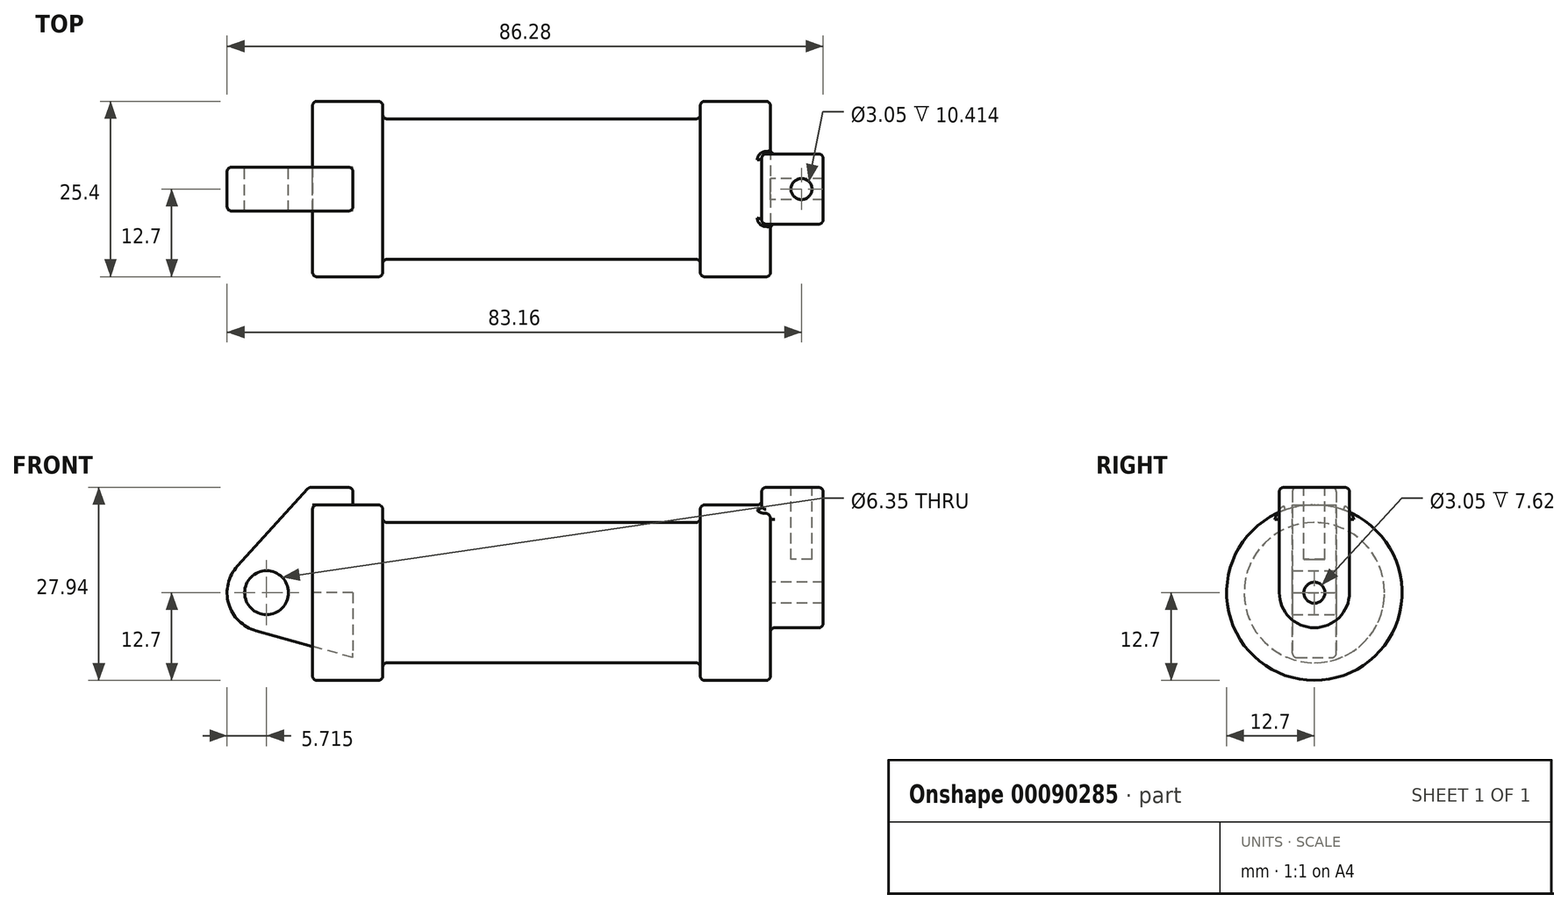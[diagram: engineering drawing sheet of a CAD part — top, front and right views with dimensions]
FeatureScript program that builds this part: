
annotation { "Feature Type Name" : "Feature", "Feature Type Description" : "" }
export const myFeature = defineFeature(function(context is Context, id is Id, definition is map)
    precondition{}
    {
        {
            var Q0;
            Q0=qCreatedBy(makeId("Front.planeOp"),FACE);
            var sketch = newSketch(context, id + "F0", { "sketchPlane" : qUnion([Q0])});
            skLineSegment(sketch, "E0", {"start": v(0, 0) * mm, "end": v(0, 12.7) * mm});
            skLineSegment(sketch, "E1", {"start": v(0, 12.7) * mm, "end": v(10.16, 12.7) * mm});
            skLineSegment(sketch, "E2", {"start": v(10.16, 12.7) * mm, "end": v(10.16, 10.16) * mm});
            skLineSegment(sketch, "E3", {"start": v(10.16, 10.16) * mm, "end": v(56.13, 10.16) * mm});
            skLineSegment(sketch, "E4", {"start": v(56.13, 10.16) * mm, "end": v(56.13, 12.7) * mm});
            skLineSegment(sketch, "E5", {"start": v(56.13, 12.7) * mm, "end": v(66.3, 12.7) * mm});
            skLineSegment(sketch, "E6", {"start": v(66.3, 12.7) * mm, "end": v(66.3, 0) * mm});
            skLineSegment(sketch, "E7", {"start": v(66.3, 0) * mm, "end": v(0, 0) * mm});
            skLineSegment(sketch, "E8", {"start": v(5.84, 15.24) * mm, "end": v(-0.5, 15.24) * mm});
            skLineSegment(sketch, "E9", {"start": v(-0.5, 15.24) * mm, "end": v(-10.88, 3.85) * mm});
            skLineSegment(sketch, "E10", {"start": v(0, 0) * mm, "end": v(-6.65, 0) * mm});
            skCircle(sketch, "E11", {"center": v(-6.65, 0) * mm, "radius": 5.72 * mm});
            skCircle(sketch, "E12", {"center": v(-6.65, 0) * mm, "radius": 3.18 * mm});
            skLineSegment(sketch, "E13", {"start": v(5.84, 15.24) * mm, "end": v(5.84, -9.4) * mm});
            skLineSegment(sketch, "E14", {"start": v(5.84, -9.4) * mm, "end": v(-8.18, -5.5) * mm});
            skSolve(sketch);
        }
        {
            var Q0;
            {var subQ0=sQuery(id+"F0.wireOp",EDGE,"E0");Q0=makeQuery(id+"F0.imprint","IMPRINT",FACE,{"disambiguationData":[TD([[makeQuery(id+"F0.imprint","IMPRINT",EDGE,{"derivedFrom":subQ0}),-1.0]])]});}
            var Q1;
            {var subQ0=sQuery(id+"F0.wireOp",EDGE,"E2");Q1=makeQuery(id+"F0.imprint","IMPRINT",FACE,{"disambiguationData":[TD([[makeQuery(id+"F0.imprint","IMPRINT",EDGE,{"derivedFrom":subQ0}),-1.0]])]});}
            var Q2;
            Q2=sQuery(id+"F0.wireOp",EDGE,"E7");
            revolve(context, id + "F1", {"entities" : qUnion([Q0, Q1]), "axis" : qUnion([Q2]), "revolveType" : RevolveType.FULL});
        }
        {
            var Q0;
            Q0=makeQuery(id+"F1.opRevolve","SWEPT_FACE",FACE,{"disambiguationData":[OSD([sQuery(id+"F0.wireOp",EDGE,"E6")])]});
            var sketch = newSketch(context, id + "F2", { "sketchPlane" : qUnion([Q0])});
            skCircle(sketch, "E15", {"center": v(0, 0) * mm, "radius": 1.52 * mm});
            skCircle(sketch, "E16", {"center": v(0, 0) * mm, "radius": 5.08 * mm});
            skLineSegment(sketch, "E17", {"start": v(-5.08, 0) * mm, "end": v(-5.08, 15.24) * mm});
            skLineSegment(sketch, "E18", {"start": v(5.08, 0) * mm, "end": v(5.08, 15.24) * mm});
            skLineSegment(sketch, "E19", {"start": v(-5.08, 15.24) * mm, "end": v(5.08, 15.24) * mm});
            skSolve(sketch);
        }
        {
            var Q0;
            Q0 = qSketchRegion(id + "F2", true);
            extrude(context, id + "F3", {"entities" : qUnion([Q0]), "operationType" : NewBodyOperationType.ADD, "depth" : 7.62 * mm});
        }
        {
            var Q0;
            Q0=makeQuery(id+"F3.opExtrude","CAP_FACE",FACE,{"disambiguationData":[OSD([sQuery(id+"F2.wireOp",EDGE,"E15"),sQuery(id+"F2.wireOp",EDGE,"E16"),sQuery(id+"F2.wireOp",EDGE,"E17"),sQuery(id+"F2.wireOp",EDGE,"E18"),sQuery(id+"F2.wireOp",EDGE,"E19")])],"isStart":true});
            extrude(context, id + "F4", {"entities" : qUnion([Q0]), "operationType" : NewBodyOperationType.ADD, "depth" : 1.27 * mm});
        }
        {
            var Q0;
            {var subQ0=sQuery(id+"F2.wireOp",EDGE,"E19");Q0=makeQuery(id+"F4.boolean.opBoolean","MERGE",FACE,{"derivedFrom":[makeQuery(id+"F3.opExtrude","SWEPT_FACE",FACE,{"disambiguationData":[OSD([subQ0])]}),makeQuery(id+"F4.opExtrude","SWEPT_FACE",FACE,{"disambiguationData":[OSD([subQ0])]})]});}
            var sketch = newSketch(context, id + "F5", { "sketchPlane" : qUnion([Q0])});
            skCircle(sketch, "E20", {"center": v(70.8, 0) * mm, "radius": 1.52 * mm});
            skSolve(sketch);
        }
        {
            var Q0;
            Q0=makeQuery(id+"F5.imprint","IMPRINT",FACE,{"disambiguationData":[TD([[makeQuery(id+"F5.imprint","IMPRINT",EDGE,{"derivedFrom":sQuery(id+"F5.wireOp",EDGE,"E20")}),1.0]])]});
            extrude(context, id + "F6", {"entities" : qUnion([Q0]), "operationType" : NewBodyOperationType.REMOVE, "oppositeDirection" : true, "depth" : 10.4 * mm});
        }
        {
            var Q0;
            {var subQ3=sQuery(id+"F0.wireOp",EDGE,"E0");Q0=makeQuery(id+"F0.imprint","IMPRINT",FACE,{"disambiguationData":[TD([[makeQuery(id+"F0.imprint","IMPRINT",EDGE,{"derivedFrom":subQ3}),1.0]])]});}
            var Q1;
            {var subQ4=sQuery(id+"F0.wireOp",EDGE,"E12");Q1=makeQuery(id+"F0.imprint","IMPRINT",FACE,{"disambiguationData":[TD([[makeQuery(id+"F0.imprint","IMPRINT",EDGE,{"derivedFrom":subQ4}),-1.0]])]});}
            var Q2;
            {var subQ0=sQuery(id+"F0.wireOp",EDGE,"E14");Q2=makeQuery(id+"F0.imprint","IMPRINT",FACE,{"disambiguationData":[TD([[makeQuery(id+"F0.imprint","IMPRINT",EDGE,{"derivedFrom":subQ0}),-1.0]])]});}
            extrude(context, id + "F7", {"entities" : qUnion([Q0, Q1, Q2]), "endBound" : BoundingType.SYMMETRIC, "depth" : 6.35 * mm});
        }
        {
            var Q0;
            Q0=makeQuery(id+"F7.opExtrude","CAP_EDGE",EDGE,{"disambiguationData":[OSD([sQuery(id+"F0.wireOp",EDGE,"E9")])],"isStart":false});
            var Q1;
            Q1=makeQuery(id+"F7.opExtrude","CAP_EDGE",EDGE,{"disambiguationData":[OSD([sQuery(id+"F0.wireOp",EDGE,"E11")])],"isStart":false});
            var Q2;
            Q2=makeQuery(id+"F7.opExtrude","CAP_EDGE",EDGE,{"disambiguationData":[OSD([sQuery(id+"F0.wireOp",EDGE,"E14")])],"isStart":false});
            var Q3;
            Q3=makeQuery(id+"F7.opExtrude","CAP_EDGE",EDGE,{"disambiguationData":[OSD([sQuery(id+"F0.wireOp",EDGE,"E8")])],"isStart":false});
            var Q4;
            {var subQ0=sQuery(id+"F0.wireOp",EDGE,"E13");Q4=makeQuery(id+"F7.opExtrude","CAP_EDGE",EDGE,{"disambiguationData":[OSD([subQ0]),TDD([makeQuery(id+"F0.imprint","IMPRINT",EDGE,{"disambiguationData":[TD([[makeQuery(id+"F0.imprint","INTERSECT",VERTEX,{"derivedFrom":[sQuery(id+"F0.wireOp",EDGE,"E8"),subQ0]}),-1.0]])],"derivedFrom":subQ0})])],"isStart":false});}
            var Q5;
            Q5=makeQuery(id+"F7.opExtrude","CAP_EDGE",EDGE,{"disambiguationData":[OSD([sQuery(id+"F0.wireOp",EDGE,"E8")])],"isStart":true});
            var Q6;
            Q6=makeQuery(id+"F7.opExtrude","SWEPT_EDGE",EDGE,{"disambiguationData":[OSD([sQuery(id+"F0.wireOp",EDGE,"E8"),sQuery(id+"F0.wireOp",EDGE,"E13")])]});
            var Q7;
            Q7=makeQuery(id+"F7.opExtrude","SWEPT_EDGE",EDGE,{"disambiguationData":[OSD([sQuery(id+"F0.wireOp",EDGE,"E8"),sQuery(id+"F0.wireOp",EDGE,"E9")])]});
            var Q8;
            Q8=makeQuery(id+"F7.opExtrude","CAP_EDGE",EDGE,{"disambiguationData":[OSD([sQuery(id+"F0.wireOp",EDGE,"E9")])],"isStart":true});
            var Q9;
            Q9=makeQuery(id+"F7.opExtrude","SWEPT_EDGE",EDGE,{"disambiguationData":[OSD([sQuery(id+"F0.wireOp",EDGE,"E9"),sQuery(id+"F0.wireOp",EDGE,"E11")])]});
            var Q10;
            Q10=makeQuery(id+"F7.opExtrude","CAP_EDGE",EDGE,{"disambiguationData":[OSD([sQuery(id+"F0.wireOp",EDGE,"E11")])],"isStart":true});
            var Q11;
            Q11=makeQuery(id+"F7.opExtrude","SWEPT_EDGE",EDGE,{"disambiguationData":[OSD([sQuery(id+"F0.wireOp",EDGE,"E11"),sQuery(id+"F0.wireOp",EDGE,"E14")])]});
            var Q12;
            Q12=makeQuery(id+"F7.opExtrude","CAP_EDGE",EDGE,{"disambiguationData":[OSD([sQuery(id+"F0.wireOp",EDGE,"E14")])],"isStart":true});
            var Q13;
            {var subQ0=sQuery(id+"F0.wireOp",EDGE,"E13");Q13=makeQuery(id+"F7.opExtrude","CAP_EDGE",EDGE,{"disambiguationData":[OSD([subQ0]),TDD([makeQuery(id+"F0.imprint","IMPRINT",EDGE,{"disambiguationData":[TD([[makeQuery(id+"F0.imprint","INTERSECT",VERTEX,{"derivedFrom":[sQuery(id+"F0.wireOp",EDGE,"E8"),subQ0]}),-1.0]])],"derivedFrom":subQ0})])],"isStart":true});}
            var Q14;
            Q14=makeQuery(id+"F1.opRevolve","SWEPT_EDGE",EDGE,{"disambiguationData":[OSD([sQuery(id+"F0.wireOp",EDGE,"E0"),sQuery(id+"F0.wireOp",EDGE,"E1")])]});
            var Q15;
            Q15=makeQuery(id+"F1.opRevolve","SWEPT_EDGE",EDGE,{"disambiguationData":[OSD([sQuery(id+"F0.wireOp",EDGE,"E1"),sQuery(id+"F0.wireOp",EDGE,"E2")])]});
            var Q16;
            Q16=makeQuery(id+"F1.opRevolve","SWEPT_FACE",FACE,{"disambiguationData":[OSD([sQuery(id+"F0.wireOp",EDGE,"E3")])]});
            var Q17;
            Q17=makeQuery(id+"F1.opRevolve","SWEPT_FACE",FACE,{"disambiguationData":[OSD([sQuery(id+"F0.wireOp",EDGE,"E1")])]});
            var Q18;
            Q18=makeQuery(id+"F1.opRevolve","SWEPT_FACE",FACE,{"disambiguationData":[OSD([sQuery(id+"F0.wireOp",EDGE,"E5")])]});
            var Q19;
            {var subQ0=sQuery(id+"F2.wireOp",EDGE,"E18");Q19=makeQuery(id+"F4.boolean.opBoolean","MERGE",FACE,{"derivedFrom":[makeQuery(id+"F3.opExtrude","SWEPT_FACE",FACE,{"disambiguationData":[OSD([subQ0])]}),makeQuery(id+"F4.opExtrude","SWEPT_FACE",FACE,{"disambiguationData":[OSD([subQ0])]})]});}
            var Q20;
            Q20=makeQuery(id+"F3.opExtrude","SWEPT_FACE",FACE,{"disambiguationData":[OSD([sQuery(id+"F2.wireOp",EDGE,"E16")])]});
            var Q21;
            {var subQ0=sQuery(id+"F2.wireOp",EDGE,"E17");Q21=makeQuery(id+"F4.boolean.opBoolean","MERGE",FACE,{"derivedFrom":[makeQuery(id+"F3.opExtrude","SWEPT_FACE",FACE,{"disambiguationData":[OSD([subQ0])]}),makeQuery(id+"F4.opExtrude","SWEPT_FACE",FACE,{"disambiguationData":[OSD([subQ0])]})]});}
            var Q22;
            {var subQ0=sQuery(id+"F2.wireOp",EDGE,"E16");var subQ1=sQuery(id+"F2.wireOp",EDGE,"E17");Q22=makeQuery(id+"F3.boolean.opBoolean","SPLIT",EDGE,{"disambiguationData":[TD([makeQuery(id+"F3.opExtrude","SWEPT_FACE",FACE,{"disambiguationData":[OSD([subQ0])]})])],"derivedFrom":makeQuery(id+"F3.opExtrude","CAP_EDGE",EDGE,{"disambiguationData":[OSD([subQ1])],"isStart":true})});}
            var Q23;
            Q23=makeQuery(id+"F4.opExtrude","CAP_EDGE",EDGE,{"disambiguationData":[OSD([sQuery(id+"F2.wireOp",EDGE,"E19")])],"isStart":false});
            var Q24;
            Q24=makeQuery(id+"F3.opExtrude","CAP_EDGE",EDGE,{"disambiguationData":[OSD([sQuery(id+"F2.wireOp",EDGE,"E19")])],"isStart":false});
            fillet(context, id + "F8", {"entities" : qUnion([Q0, Q1, Q2, Q3, Q4, Q5, Q6, Q7, Q8, Q9, Q10, Q11, Q12, Q13, Q14, Q15, Q16, Q17, Q18, Q19, Q20, Q21, Q22, Q23, Q24]), "radius" : 0.64 * mm, "allowEdgeOverflow" : false});
        }
    });
